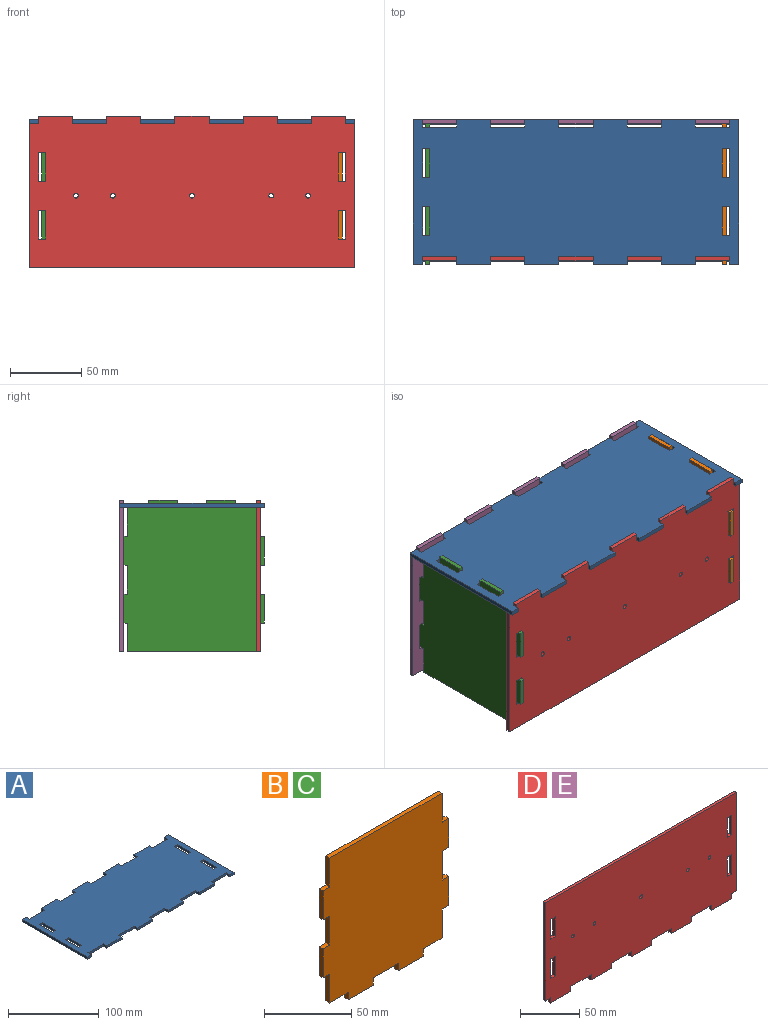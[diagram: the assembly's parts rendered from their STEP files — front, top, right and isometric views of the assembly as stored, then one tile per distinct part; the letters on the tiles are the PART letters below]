
ASSEMBLY  parts=5 mates=4
PART A: 62 faces, bbox 228.6x101.6x2.9 mm
  f0: plane 5.21x2.92mm, normal (0,-1,0), area 15.2mm2, adj f1,f59,f60,f61
  f1: plane 20.32x2.92mm, normal (-1,0,0), area 59.4mm2, adj f0,f2,f60,f61
  f2: plane 5.21x2.92mm, normal (0,1,0), area 15.2mm2, adj f1,f59,f60,f61
  f3: plane 5.21x2.92mm, normal (0,-1,0), area 15.2mm2, adj f4,f55,f60,f61
  f4: plane 20.32x2.92mm, normal (-1,0,0), area 59.4mm2, adj f3,f5,f60,f61
  f5: plane 5.21x2.92mm, normal (0,1,0), area 15.2mm2, adj f4,f55,f60,f61
  f6: plane 6.35x2.92mm, normal (0,-1,0), area 18.5mm2, adj f7,f56,f60,f61
  f7: plane 101.6x2.92mm, normal (1,0,0), area 296.8mm2, adj f6,f8,f60,f61
  f8: plane 6.35x2.92mm, normal (0,1,0), area 18.5mm2, adj f7,f9,f60,f61
  f9: plane 5.21x2.92mm, normal (-1,0,0), area 15.2mm2, adj f8,f10,f60,f61
  f10: plane 23.99x2.92mm, normal (0,1,0), area 70.1mm2, adj f9,f11,f60,f61
  f11: plane 5.21x2.92mm, normal (1,0,0), area 15.2mm2, adj f10,f12,f60,f61
  f12: plane 23.99x2.92mm, normal (0,1,0), area 70.1mm2, adj f11,f13,f60,f61
  f13: plane 5.21x2.92mm, normal (-1,0,0), area 15.2mm2, adj f12,f14,f60,f61
  f14: plane 23.99x2.92mm, normal (0,1,0), area 70.1mm2, adj f13,f15,f60,f61
  f15: plane 5.21x2.92mm, normal (1,0,0), area 15.2mm2, adj f14,f16,f60,f61
  f16: plane 23.99x2.92mm, normal (0,1,0), area 70.1mm2, adj f15,f17,f60,f61
  f17: plane 5.21x2.92mm, normal (-1,0,0), area 15.2mm2, adj f16,f18,f60,f61
  f18: plane 23.99x2.92mm, normal (0,1,0), area 70.1mm2, adj f17,f19,f60,f61
  f19: plane 5.21x2.92mm, normal (1,0,0), area 15.2mm2, adj f18,f20,f60,f61
  f20: plane 23.99x2.92mm, normal (0,1,0), area 70.1mm2, adj f19,f21,f60,f61
  f21: plane 5.21x2.92mm, normal (-1,0,0), area 15.2mm2, adj f20,f22,f60,f61
  f22: plane 23.99x2.92mm, normal (0,1,0), area 70.1mm2, adj f21,f23,f60,f61
  f23: plane 5.21x2.92mm, normal (1,0,0), area 15.2mm2, adj f22,f24,f60,f61
  f24: plane 23.99x2.92mm, normal (0,1,0), area 70.1mm2, adj f23,f25,f60,f61
  f25: plane 5.21x2.92mm, normal (-1,0,0), area 15.2mm2, adj f24,f26,f60,f61
  f26: plane 23.99x2.92mm, normal (0,1,0), area 70.1mm2, adj f25,f27,f60,f61
  f27: plane 5.21x2.92mm, normal (1,0,0), area 15.2mm2, adj f26,f28,f60,f61
  f28: plane 6.35x2.92mm, normal (0,1,0), area 18.5mm2, adj f27,f29,f60,f61
  f29: plane 101.6x2.92mm, normal (-1,0,0), area 296.8mm2, adj f28,f30,f60,f61
  f30: plane 6.35x2.92mm, normal (0,-1,0), area 18.5mm2, adj f29,f31,f60,f61
  f31: plane 5.21x2.92mm, normal (1,0,0), area 15.2mm2, adj f30,f32,f60,f61
  f32: plane 23.99x2.92mm, normal (0,-1,0), area 70.1mm2, adj f31,f33,f60,f61
  f33: plane 5.21x2.92mm, normal (-1,0,0), area 15.2mm2, adj f32,f34,f60,f61
  f34: plane 23.99x2.92mm, normal (0,-1,0), area 70.1mm2, adj f33,f35,f60,f61
  f35: plane 5.21x2.92mm, normal (1,0,0), area 15.2mm2, adj f34,f36,f60,f61
  f36: plane 23.99x2.92mm, normal (0,-1,0), area 70.1mm2, adj f35,f37,f60,f61
  f37: plane 5.21x2.92mm, normal (-1,0,0), area 15.2mm2, adj f36,f38,f60,f61
  f38: plane 23.99x2.92mm, normal (0,-1,0), area 70.1mm2, adj f37,f39,f60,f61
  f39: plane 5.21x2.92mm, normal (1,0,0), area 15.2mm2, adj f38,f40,f60,f61
  f40: plane 23.99x2.92mm, normal (0,-1,0), area 70.1mm2, adj f39,f41,f60,f61
  f41: plane 5.21x2.92mm, normal (-1,0,0), area 15.2mm2, adj f40,f42,f60,f61
  f42: plane 23.99x2.92mm, normal (0,-1,0), area 70.1mm2, adj f41,f43,f60,f61
  f43: plane 5.21x2.92mm, normal (1,0,0), area 15.2mm2, adj f42,f44,f60,f61
  f44: plane 23.99x2.92mm, normal (0,-1,0), area 70.1mm2, adj f43,f45,f60,f61
  f45: plane 5.21x2.92mm, normal (-1,0,0), area 15.2mm2, adj f44,f46,f60,f61
  f46: plane 23.99x2.92mm, normal (0,-1,0), area 70.1mm2, adj f45,f47,f60,f61
  f47: plane 5.21x2.92mm, normal (1,0,0), area 15.2mm2, adj f46,f48,f60,f61
  f48: plane 23.99x2.92mm, normal (0,-1,0), area 70.1mm2, adj f47,f56,f60,f61
  f49: plane 20.32x2.92mm, normal (1,0,0), area 59.4mm2, adj f50,f57,f60,f61
  f50: plane 5.21x2.92mm, normal (0,-1,0), area 15.2mm2, adj f49,f51,f60,f61
  f51: plane 20.32x2.92mm, normal (-1,0,0), area 59.4mm2, adj f50,f57,f60,f61
  f52: plane 20.32x2.92mm, normal (1,0,0), area 59.4mm2, adj f53,f58,f60,f61
  f53: plane 5.21x2.92mm, normal (0,-1,0), area 15.2mm2, adj f52,f54,f60,f61
  f54: plane 20.32x2.92mm, normal (-1,0,0), area 59.4mm2, adj f53,f58,f60,f61
  f55: plane 20.32x2.92mm, normal (1,0,0), area 59.4mm2, adj f3,f5,f60,f61
  f56: plane 5.21x2.92mm, normal (-1,0,0), area 15.2mm2, adj f6,f48,f60,f61
  f57: plane 5.21x2.92mm, normal (0,1,0), area 15.2mm2, adj f49,f51,f60,f61
  f58: plane 5.21x2.92mm, normal (0,1,0), area 15.2mm2, adj f52,f54,f60,f61
  f59: plane 20.32x2.92mm, normal (1,0,0), area 59.4mm2, adj f0,f2,f60,f61
  f60: plane 228.6x101.6mm, normal (0,0,1), area 21553.4mm2, adj f0,f1,f2,f3,f4,f5,f6,f7
  f61: plane 228.6x101.6mm, normal (0,0,-1), area 21553.4mm2, adj f0,f1,f2,f3,f4,f5,f6,f7
PART B: 30 faces, bbox 101.6x2.9x106.8 mm
  f0: plane 20.32x2.92mm, normal (1,0,0), area 59.4mm2, adj f1,f27,f28,f29
  f1: plane 5.21x2.92mm, normal (0,0,-1), area 15.2mm2, adj f0,f2,f28,f29
  f2: plane 20.32x2.92mm, normal (1,0,0), area 59.4mm2, adj f1,f3,f28,f29
  f3: plane 5.21x2.92mm, normal (0,0,1), area 15.2mm2, adj f2,f4,f28,f29
  f4: plane 20.32x2.92mm, normal (1,0,0), area 59.4mm2, adj f3,f5,f28,f29
  f5: plane 5.21x2.92mm, normal (0,0,-1), area 15.2mm2, adj f4,f6,f28,f29
  f6: plane 20.32x2.92mm, normal (1,0,0), area 59.4mm2, adj f5,f7,f28,f29
  f7: plane 5.21x2.92mm, normal (0,0,1), area 15.2mm2, adj f6,f8,f28,f29
  f8: plane 20.32x2.92mm, normal (1,0,0), area 59.4mm2, adj f7,f9,f28,f29
  f9: plane 91.19x2.92mm, normal (0,0,1), area 266.4mm2, adj f8,f10,f28,f29
  f10: plane 20.32x2.92mm, normal (-1,0,0), area 59.4mm2, adj f9,f11,f28,f29
  f11: plane 5.21x2.92mm, normal (0,0,1), area 15.2mm2, adj f10,f12,f28,f29
  f12: plane 20.32x2.92mm, normal (-1,0,0), area 59.4mm2, adj f11,f13,f28,f29
  f13: plane 5.21x2.92mm, normal (0,0,-1), area 15.2mm2, adj f12,f14,f28,f29
  f14: plane 20.32x2.92mm, normal (-1,0,0), area 59.4mm2, adj f13,f15,f28,f29
  f15: plane 5.21x2.92mm, normal (0,0,1), area 15.2mm2, adj f14,f16,f28,f29
  f16: plane 20.32x2.92mm, normal (-1,0,0), area 59.4mm2, adj f15,f17,f28,f29
  f17: plane 5.21x2.92mm, normal (0,0,-1), area 15.2mm2, adj f16,f18,f28,f29
  f18: plane 20.32x2.92mm, normal (-1,0,0), area 59.4mm2, adj f17,f19,f28,f29
  f19: plane 15.11x2.92mm, normal (0,0,-1), area 44.1mm2, adj f18,f20,f28,f29
  f20: plane 5.21x2.92mm, normal (-1,0,0), area 15.2mm2, adj f19,f21,f28,f29
  f21: plane 20.32x2.92mm, normal (0,0,-1), area 59.4mm2, adj f20,f22,f28,f29
  f22: plane 5.21x2.92mm, normal (1,0,0), area 15.2mm2, adj f21,f23,f28,f29
  f23: plane 20.32x2.92mm, normal (0,0,-1), area 59.4mm2, adj f22,f24,f28,f29
  f24: plane 5.21x2.92mm, normal (-1,0,0), area 15.2mm2, adj f23,f25,f28,f29
  f25: plane 20.32x2.92mm, normal (0,0,-1), area 59.4mm2, adj f24,f26,f28,f29
  f26: plane 5.21x2.92mm, normal (1,0,0), area 15.2mm2, adj f25,f27,f28,f29
  f27: plane 15.11x2.92mm, normal (0,0,-1), area 44.1mm2, adj f0,f26,f28,f29
  f28: plane 106.81x101.6mm, normal (0,-1,0), area 9899.3mm2, adj f0,f1,f2,f3,f4,f5,f6,f7
  f29: plane 106.81x101.6mm, normal (0,1,0), area 9899.3mm2, adj f0,f1,f2,f3,f4,f5,f6,f7
PART C: same geometry as B
PART D: 47 faces, bbox 228.6x2.9x106.8 mm
  f0: plane 20.32x2.92mm, normal (-1,0,0), area 59.4mm2, adj f1,f39,f45,f46
  f1: plane 5.21x2.92mm, normal (0,0,1), area 15.2mm2, adj f0,f2,f45,f46
  f2: plane 20.32x2.92mm, normal (1,0,0), area 59.4mm2, adj f1,f39,f45,f46
  f3: plane 5.21x2.92mm, normal (0,0,-1), area 15.2mm2, adj f4,f40,f45,f46
  f4: plane 20.32x2.92mm, normal (-1,0,0), area 59.4mm2, adj f3,f5,f45,f46
  f5: plane 5.21x2.92mm, normal (0,0,1), area 15.2mm2, adj f4,f40,f45,f46
  f6: plane 20.32x2.92mm, normal (1,0,0), area 59.4mm2, adj f7,f41,f45,f46
  f7: plane 5.21x2.92mm, normal (0,0,-1), area 15.2mm2, adj f6,f8,f45,f46
  f8: plane 20.32x2.92mm, normal (-1,0,0), area 59.4mm2, adj f7,f41,f45,f46
  f9: plane 20.32x2.92mm, normal (1,0,0), area 59.4mm2, adj f10,f42,f45,f46
  f10: plane 5.21x2.92mm, normal (0,0,-1), area 15.2mm2, adj f9,f11,f45,f46
  f11: plane 20.32x2.92mm, normal (-1,0,0), area 59.4mm2, adj f10,f42,f45,f46
  f12: plane 5.21x2.92mm, normal (1,0,0), area 15.2mm2, adj f13,f43,f45,f46
  f13: plane 23.99x2.92mm, normal (0,0,-1), area 70.1mm2, adj f12,f14,f45,f46
  f14: plane 5.21x2.92mm, normal (-1,0,0), area 15.2mm2, adj f13,f15,f45,f46
  f15: plane 23.99x2.92mm, normal (0,0,-1), area 70.1mm2, adj f14,f16,f45,f46
  f16: plane 5.21x2.92mm, normal (1,0,0), area 15.2mm2, adj f15,f17,f45,f46
  f17: plane 23.99x2.92mm, normal (0,0,-1), area 70.1mm2, adj f16,f18,f45,f46
  f18: plane 5.21x2.92mm, normal (-1,0,0), area 15.2mm2, adj f17,f19,f45,f46
  f19: plane 23.99x2.92mm, normal (0,0,-1), area 70.1mm2, adj f18,f20,f45,f46
  f20: plane 5.21x2.92mm, normal (1,0,0), area 15.2mm2, adj f19,f21,f45,f46
  f21: plane 23.99x2.92mm, normal (0,0,-1), area 70.1mm2, adj f20,f22,f45,f46
  f22: plane 5.21x2.92mm, normal (-1,0,0), area 15.2mm2, adj f21,f23,f45,f46
  f23: plane 23.99x2.92mm, normal (0,0,-1), area 70.1mm2, adj f22,f24,f45,f46
  f24: plane 5.21x2.92mm, normal (1,0,0), area 15.2mm2, adj f23,f25,f45,f46
  f25: plane 23.99x2.92mm, normal (0,0,-1), area 70.1mm2, adj f24,f26,f45,f46
  f26: plane 5.21x2.92mm, normal (-1,0,0), area 15.2mm2, adj f25,f27,f45,f46
  f27: plane 23.99x2.92mm, normal (0,0,-1), area 70.1mm2, adj f26,f28,f45,f46
  f28: plane 5.21x2.92mm, normal (1,0,0), area 15.2mm2, adj f27,f29,f45,f46
  f29: plane 6.35x2.92mm, normal (0,0,-1), area 18.5mm2, adj f28,f30,f45,f46
  f30: plane 101.6x2.92mm, normal (1,0,0), area 296.8mm2, adj f29,f31,f45,f46
  f31: plane 228.6x2.92mm, normal (0,0,1), area 667.7mm2, adj f30,f32,f45,f46
  f32: plane 101.6x2.92mm, normal (-1,0,0), area 296.8mm2, adj f31,f33,f45,f46
  f33: plane 6.35x2.92mm, normal (0,0,-1), area 18.5mm2, adj f32,f34,f45,f46
  f34: plane 5.21x2.92mm, normal (-1,0,0), area 15.2mm2, adj f33,f43,f45,f46
  f35: cylinder r=1.59mm len=3.18mm, axis (0,1,0), area 29.1mm2, adj f45,f46
  f36: cylinder r=1.65mm len=3.3mm, axis (0,1,0), area 30.3mm2, adj f45,f46
  f37: cylinder r=1.65mm len=3.3mm, axis (0,1,0), area 30.3mm2, adj f45,f46
  f38: cylinder r=1.65mm len=3.3mm, axis (0,1,0), area 30.3mm2, adj f45,f46
  f39: plane 5.21x2.92mm, normal (0,0,-1), area 15.2mm2, adj f0,f2,f45,f46
  f40: plane 20.32x2.92mm, normal (1,0,0), area 59.4mm2, adj f3,f5,f45,f46
  f41: plane 5.21x2.92mm, normal (0,0,1), area 15.2mm2, adj f6,f8,f45,f46
  f42: plane 5.21x2.92mm, normal (0,0,1), area 15.2mm2, adj f9,f11,f45,f46
  f43: plane 23.99x2.92mm, normal (0,0,-1), area 70.1mm2, adj f12,f34,f45,f46
  f44: cylinder r=1.65mm len=3.3mm, axis (0,1,0), area 30.3mm2, adj f45,f46
  f45: plane 228.6x106.81mm, normal (0,-1,0), area 23384.9mm2, adj f0,f1,f2,f3,f4,f5,f6,f7
  f46: plane 228.6x106.81mm, normal (0,1,0), area 23384.9mm2, adj f0,f1,f2,f3,f4,f5,f6,f7
PART E: same geometry as D
PLACE A t=(0.44,4.07,-3.3)mm fixed
PLACE B rot(axis=(0.71,-0.71,0),180deg) t=(103.18,-0.21,-54.1)mm
PLACE C rot(axis=(-0.71,-0.71,0),180deg) t=(-102.3,-0.21,-54.1)mm
PLACE D rot(axis=(0,1,0),180deg) t=(0.44,-45.8,-54.1)mm
PLACE E rot(axis=(0,-1,0),180deg) t=(0.44,50.59,-54.1)mm
MATE parallel C.f26 <-> A.f50  axis (0,1,0) through (-103.76,30.27,-0.7)mm
MATE parallel A.f27 <-> E.f28  axis (1,0,0) through (-107.51,47.99,-1.84)mm
MATE parallel B.f22 <-> A.f5  axis (0,-1,0) through (104.64,9.95,-0.7)mm
MATE parallel D.f16 <-> A.f43  axis (-1,0,0) through (36.42,-47.26,-0.7)mm
